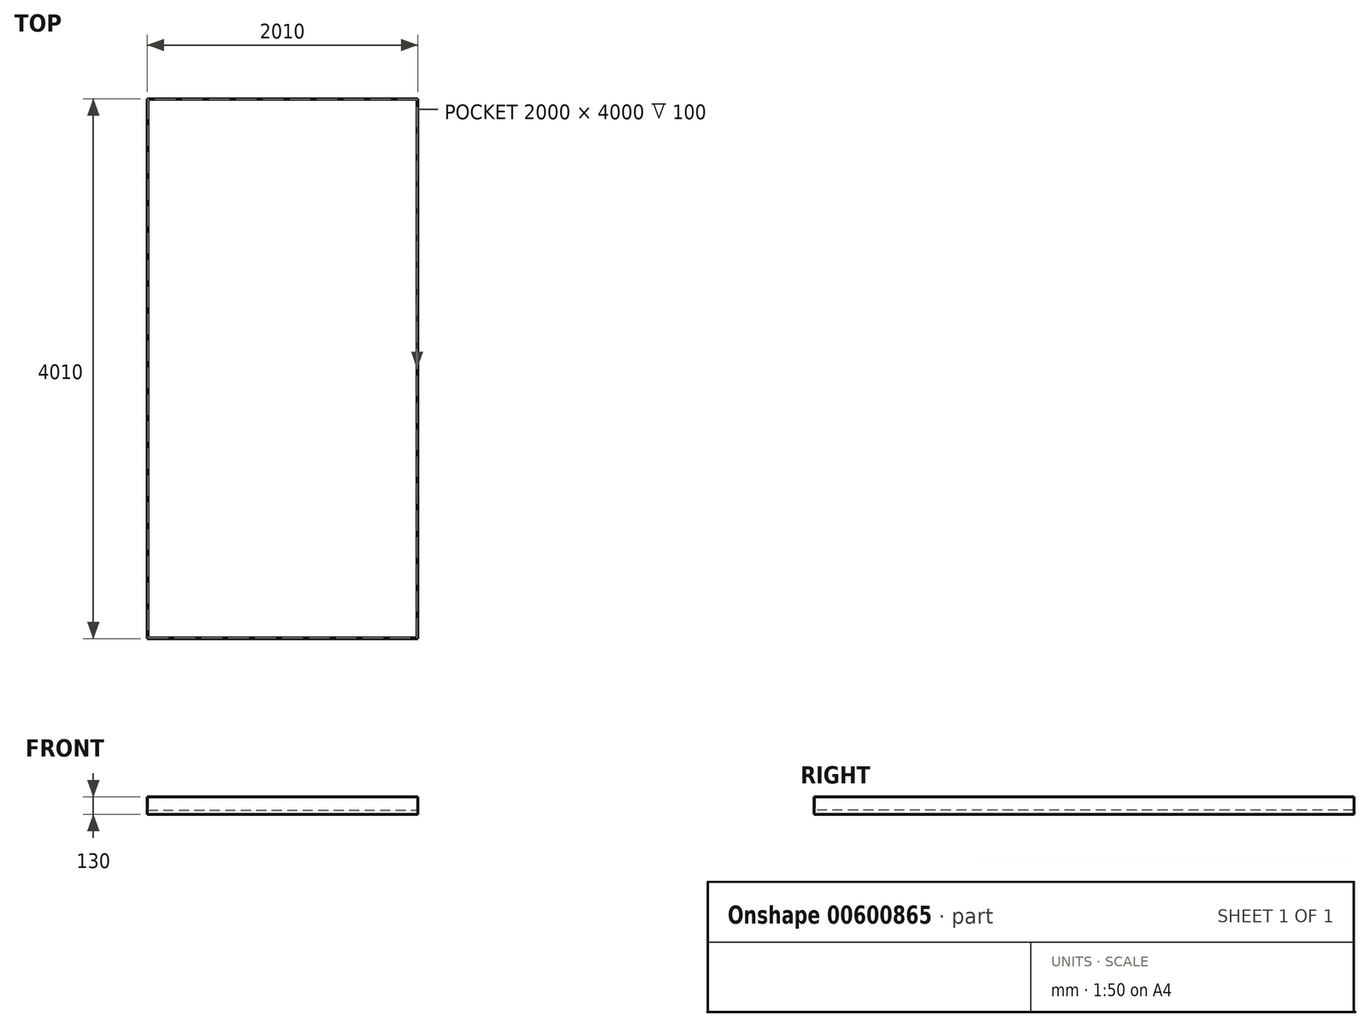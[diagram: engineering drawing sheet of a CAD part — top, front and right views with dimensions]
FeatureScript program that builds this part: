
annotation { "Feature Type Name" : "Feature", "Feature Type Description" : "" }
export const myFeature = defineFeature(function(context is Context, id is Id, definition is map)
    precondition{}
    {
        {
            var Q0;
            Q0=qCreatedBy(makeId("Top.planeOp"),FACE);
            var sketch = newSketch(context, id + "F0", { "sketchPlane" : qUnion([Q0])});
            skLineSegment(sketch, "E0.bottom", {"start": v(0, 0) * mm, "end": v(2010, 0) * mm});
            skLineSegment(sketch, "E0.top", {"start": v(0, 4010) * mm, "end": v(2010, 4010) * mm});
            skLineSegment(sketch, "E0.left", {"start": v(0, 0) * mm, "end": v(0, 4010) * mm});
            skLineSegment(sketch, "E0.right", {"start": v(2010, 0) * mm, "end": v(2010, 4010) * mm});
            skSolve(sketch);
        }
        {
            var Q0;
            Q0=makeQuery(id+"F0.imprint","IMPRINT",FACE,{"disambiguationData":[TD([[makeQuery(id+"F0.imprint","IMPRINT",EDGE,{"derivedFrom":sQuery(id+"F0.wireOp",EDGE,"E0.bottom")}),1.0]])]});
            extrude(context, id + "F1", {"entities" : qUnion([Q0]), "depth" : 30 * mm, "offsetDistance" : 25 * mm});
        }
        {
            var Q0;
            Q0=makeQuery(id+"F1.opExtrude","CAP_FACE",FACE,{"disambiguationData":[OSD([sQuery(id+"F0.wireOp",EDGE,"E0.bottom"),sQuery(id+"F0.wireOp",EDGE,"E0.top"),sQuery(id+"F0.wireOp",EDGE,"E0.left"),sQuery(id+"F0.wireOp",EDGE,"E0.right")])],"isStart":false});
            var sketch = newSketch(context, id + "F2", { "sketchPlane" : qUnion([Q0])});
            skLineSegment(sketch, "E1.0", {"start": v(0, 0) * mm, "end": v(0, 4010) * mm});
            skLineSegment(sketch, "E2.0", {"start": v(0, 0) * mm, "end": v(2010, 0) * mm});
            skLineSegment(sketch, "E3.0", {"start": v(2010, 0) * mm, "end": v(2010, 4010) * mm});
            skLineSegment(sketch, "E4.0", {"start": v(0, 4010) * mm, "end": v(2010, 4010) * mm});
            skLineSegment(sketch, "E5.bottom", {"start": v(5, 4005) * mm, "end": v(2005, 4005) * mm});
            skLineSegment(sketch, "E5.top", {"start": v(5, 5) * mm, "end": v(2005, 5) * mm});
            skLineSegment(sketch, "E5.left", {"start": v(5, 4005) * mm, "end": v(5, 5) * mm});
            skLineSegment(sketch, "E5.right", {"start": v(2005, 4005) * mm, "end": v(2005, 5) * mm});
            skSolve(sketch);
        }
        {
            var Q0;
            Q0=makeQuery(id+"F2.imprint","IMPRINT",FACE,{"disambiguationData":[TD([[makeQuery(id+"F2.imprint","IMPRINT",EDGE,{"derivedFrom":sQuery(id+"F2.wireOp",EDGE,"E1.0")}),-1.0]])]});
            extrude(context, id + "F3", {"entities" : qUnion([Q0]), "operationType" : NewBodyOperationType.ADD, "depth" : 100 * mm, "offsetDistance" : 25 * mm});
        }
    });
